# Revit family: Electrical_Equipment-Room_Controller-HCS-NXRC_Series
name_source: partatom
category: Data Devices
revit_build: Autodesk Revit 2014 (Build: 20130308_1515(x64)
units: mm (PartAtom-declared; Revit-internal decimal feet)

## types (1)
- NXRC Series
    Apparent Load = 0.000 VA
    Assembly Code = D5030
    Certifications = Title 24, c UL us
    Connector Description 1 = Power Supply
    Connector Description 2 = Communication
    Construction = GSM UL Rated 94 HB Plastic
    Default Elevation = 48 "
    Description = Room Controller
    Device Material = Hubbell - Blue
    Dimming = 0-10VDC, 60mA per channel; For use with low voltage, two-wire dimming ballast and LED drivers
    Electrical Rating Input = 120/277/347VAC, 20A Max, 50/60 Hz; Single feed connection regardless of one or two relays
    Load Classification = Other
    Manufacturer = Hubbell Control Solutions
    Model = NXRC Series
    Mounting = Mounts directly to an external junction box through an extended 1/2” chase nipple
    Operating Temperature = 32°F to 104°F [0°C to 40°C]
    Plenum rated = Complies with requirements fore use in a plenum area; Plenum rated for external junction box mounting
    Power Factor = 1
    Product Documentation Link = https://hubbellcdn.com
    Product Page URL = https://www.hubbell.com
    Relative humidity = 0 to 95%
    Type Comments = Data Devices
    URL = https://www.hubbell.com
    Voltage = 120 V
    Warranty = Five-year limited
    Weight = 0 kg

## geometry (parser evidence)
native form markers: Sweep x2
no freeform markers — native parametric forms only
